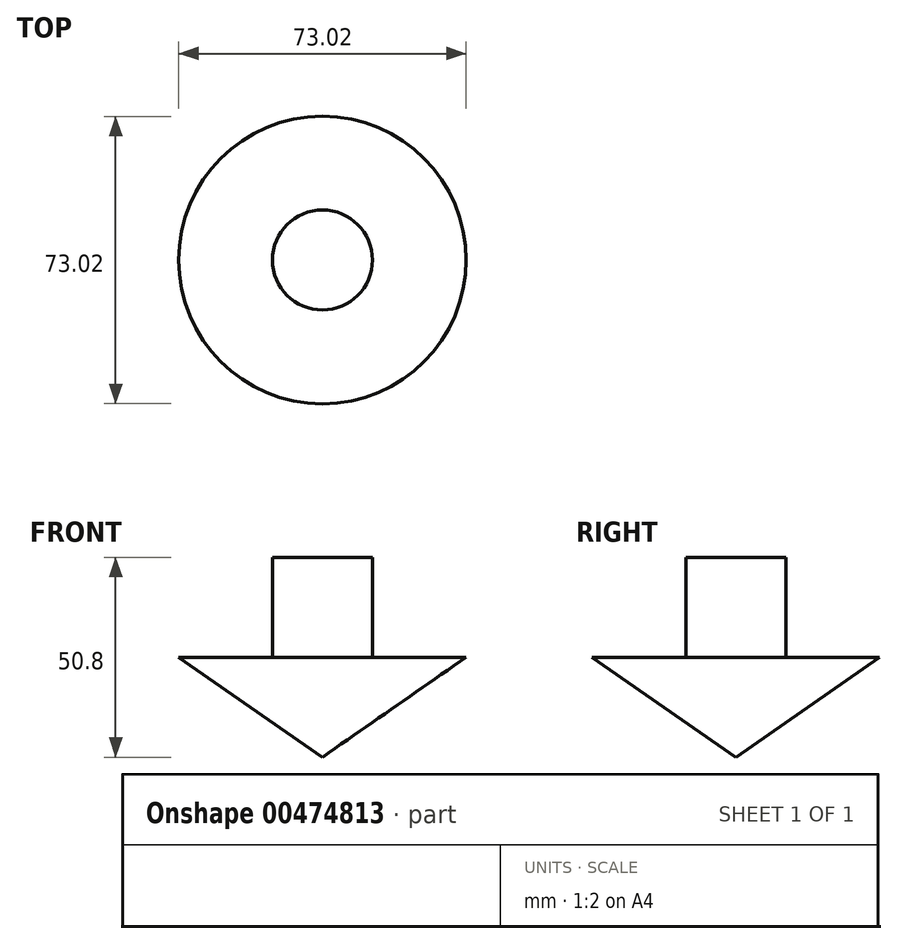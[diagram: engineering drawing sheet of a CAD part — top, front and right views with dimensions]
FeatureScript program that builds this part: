
annotation { "Feature Type Name" : "Feature", "Feature Type Description" : "" }
export const myFeature = defineFeature(function(context is Context, id is Id, definition is map)
    precondition{}
    {
        {
            var Q0;
            Q0=qCreatedBy(makeId("Front.planeOp"),FACE);
            var sketch = newSketch(context, id + "F0", { "sketchPlane" : qUnion([Q0])});
            skLineSegment(sketch, "E0", {"start": v(0, 0) * mm, "end": v(36.51, 25.4) * mm});
            skLineSegment(sketch, "E1", {"start": v(36.51, 25.4) * mm, "end": v(12.7, 25.4) * mm});
            skLineSegment(sketch, "E2", {"start": v(12.7, 25.4) * mm, "end": v(12.7, 50.8) * mm});
            skLineSegment(sketch, "E3", {"start": v(12.7, 50.8) * mm, "end": v(0, 50.8) * mm});
            skLineSegment(sketch, "E4", {"start": v(0, 50.8) * mm, "end": v(0, 0) * mm});
            skSolve(sketch);
        }
        {
            var Q0;
            Q0=makeQuery(id+"F0.imprint","IMPRINT",FACE,{"disambiguationData":[TD([[makeQuery(id+"F0.imprint","IMPRINT",EDGE,{"derivedFrom":sQuery(id+"F0.wireOp",EDGE,"E0")}),1.0]])]});
            var Q1;
            Q1=sQuery(id+"F0.wireOp",EDGE,"E4");
            revolve(context, id + "F1", {"entities" : qUnion([Q0]), "axis" : qUnion([Q1]), "revolveType" : RevolveType.FULL});
        }
    });
